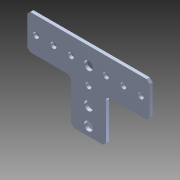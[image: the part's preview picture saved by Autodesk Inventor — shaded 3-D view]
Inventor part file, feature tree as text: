
AUTODESK INVENTOR PART (.ipt)
format: ipt  version: 2015 SP1 (Build 190203100, 203)  size: 179,712 bytes
history: native  units: in
note: dims shown in document units (in); Inventor stores cm internally (conversion verified against a paired STEP export)
features: extrude x2, sketch x2, projected_geometry x2, fillet x1, other x1, imported_body x1
ambient origin geometry x8: Origin, YZ Plane, XZ Plane, XY Plane, X Axis, Y Axis, Z Axis, Center Point
bodies: Body1 (feature_tree)
feature tree (9):
  fillet  "Fillet1"  Radius=0.25in
  other  "VersaFrame Gusset (217-3557)1"
  extrude  "Extrusion1"  Depth=1.0in TaperAngle=0.0deg
  extrude  "Extrusion3"  Depth=1.0in TaperAngle=0.0deg
  imported_body  "Base1"
  sketch  "Sketch1"  dims[d1=0.25in d2=1.0in d3=0.0in]
  projected_geometry  "Projected Loop1"
  sketch  "Sketch3"  dims[d8=0.25in d9=1.0in d10=0.0in]
  projected_geometry  "Projected Loop3"
